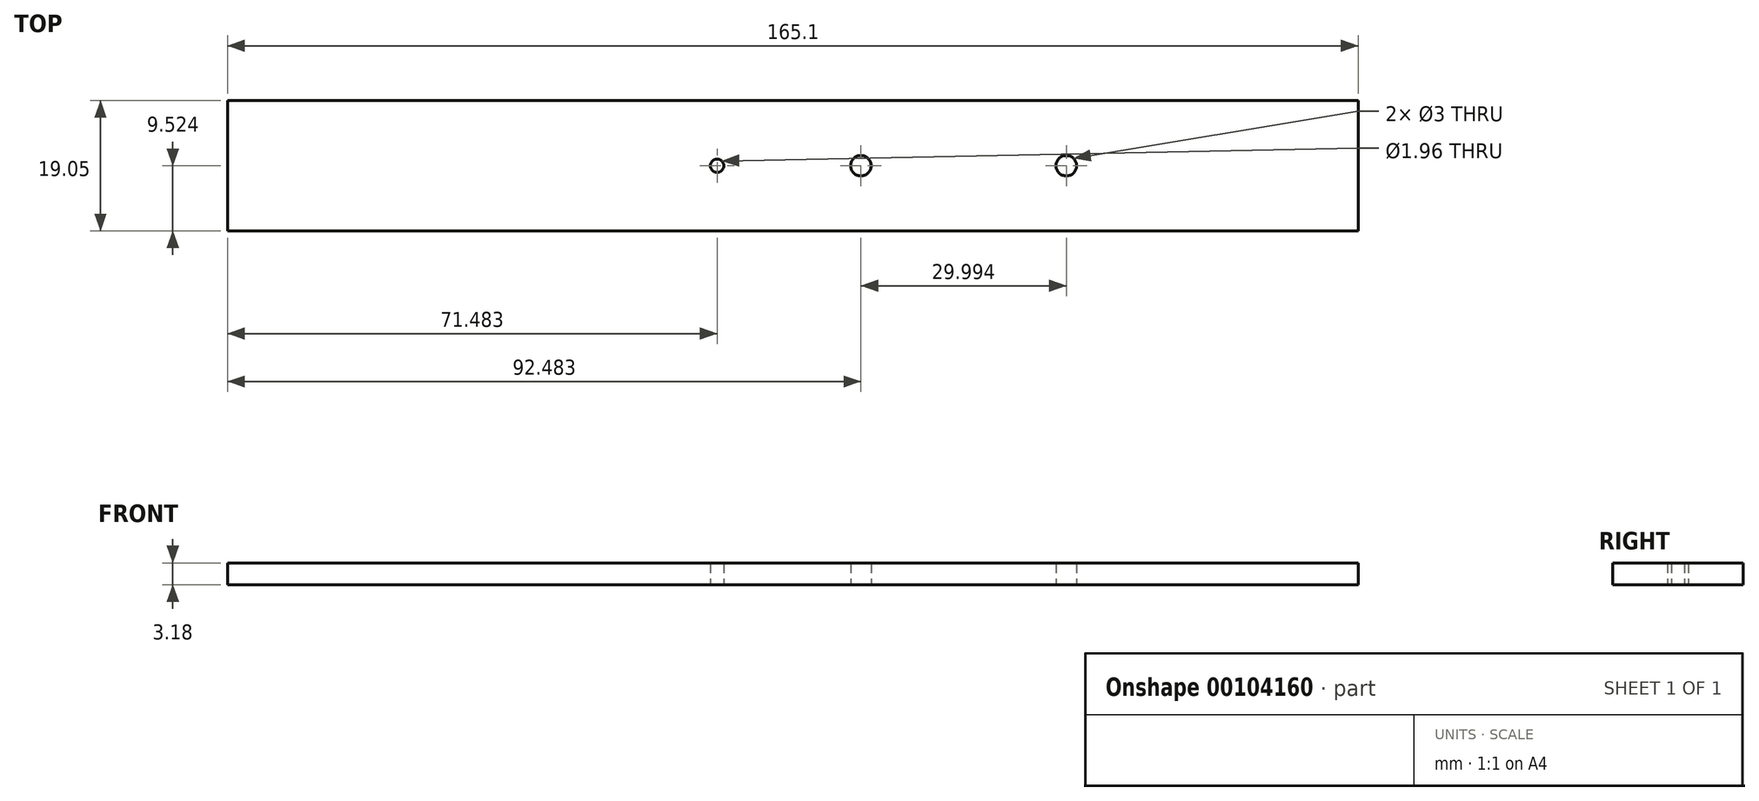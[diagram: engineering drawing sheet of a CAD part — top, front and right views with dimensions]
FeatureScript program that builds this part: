
annotation { "Feature Type Name" : "Feature", "Feature Type Description" : "" }
export const myFeature = defineFeature(function(context is Context, id is Id, definition is map)
    precondition{}
    {
        {
            var Q0;
            Q0=qCreatedBy(makeId("Top.planeOp"),FACE);
            var sketch = newSketch(context, id + "F0", { "sketchPlane" : qUnion([Q0])});
            skLineSegment(sketch, "E0.bottom", {"start": v(-131.62, -9.37) * mm, "end": v(33.48, -9.37) * mm});
            skLineSegment(sketch, "E0.top", {"start": v(-131.62, -28.42) * mm, "end": v(33.48, -28.42) * mm});
            skLineSegment(sketch, "E0.left", {"start": v(-131.62, -9.37) * mm, "end": v(-131.62, -28.42) * mm});
            skLineSegment(sketch, "E0.right", {"start": v(33.48, -9.37) * mm, "end": v(33.48, -28.42) * mm});
            skSolve(sketch);
        }
        {
            var Q0;
            Q0=makeQuery(id+"F0.imprint","IMPRINT",FACE,{"disambiguationData":[TD([[makeQuery(id+"F0.imprint","IMPRINT",EDGE,{"derivedFrom":sQuery(id+"F0.wireOp",EDGE,"E0.bottom")}),-1.0]])]});
            extrude(context, id + "F1", {"entities" : qUnion([Q0]), "depth" : 3.17 * mm});
        }
        {
            var Q0;
            Q0=makeQuery(id+"F1.opExtrude","CAP_FACE",FACE,{"disambiguationData":[OSD([sQuery(id+"F0.wireOp",EDGE,"E0.bottom"),sQuery(id+"F0.wireOp",EDGE,"E0.top"),sQuery(id+"F0.wireOp",EDGE,"E0.left"),sQuery(id+"F0.wireOp",EDGE,"E0.right")])],"isStart":true});
            var sketch = newSketch(context, id + "F2", { "sketchPlane" : qUnion([Q0])});
            skCircle(sketch, "E1", {"center": v(-39.14, 18.9) * mm, "radius": 1.5 * mm});
            skCircle(sketch, "E2", {"center": v(-60.14, 18.9) * mm, "radius": 0.98 * mm});
            skLineSegment(sketch, "E3.bottom", {"start": v(8.08, 12.93) * mm, "end": v(-14.14, 12.93) * mm});
            skLineSegment(sketch, "E3.top", {"start": v(8.08, 24.86) * mm, "end": v(-14.14, 24.86) * mm});
            skLineSegment(sketch, "E3.left", {"start": v(8.08, 12.93) * mm, "end": v(8.08, 24.86) * mm});
            skLineSegment(sketch, "E3.right", {"start": v(-14.14, 12.93) * mm, "end": v(-14.14, 24.86) * mm});
            skCircle(sketch, "E4", {"center": v(-9.14, 18.9) * mm, "radius": 1.5 * mm});
            skSolve(sketch);
        }
        {
            var Q0;
            Q0=makeQuery(id+"F2.imprint","IMPRINT",FACE,{"disambiguationData":[TD([[makeQuery(id+"F2.imprint","IMPRINT",EDGE,{"derivedFrom":sQuery(id+"F2.wireOp",EDGE,"E1")}),1.0]])]});
            extrude(context, id + "F3", {"entities" : qUnion([Q0]), "operationType" : NewBodyOperationType.REMOVE, "oppositeDirection" : true, "depth" : 25.4 * mm});
        }
        {
            var Q0;
            Q0=makeQuery(id+"F2.imprint","IMPRINT",FACE,{"disambiguationData":[TD([[makeQuery(id+"F2.imprint","IMPRINT",EDGE,{"derivedFrom":sQuery(id+"F2.wireOp",EDGE,"E2")}),1.0]])]});
            extrude(context, id + "F4", {"entities" : qUnion([Q0]), "operationType" : NewBodyOperationType.REMOVE, "oppositeDirection" : true, "depth" : 25.4 * mm});
        }
        {
            var Q0;
            Q0=makeQuery(id+"F2.imprint","IMPRINT",FACE,{"disambiguationData":[TD([[makeQuery(id+"F2.imprint","IMPRINT",EDGE,{"derivedFrom":sQuery(id+"F2.wireOp",EDGE,"E4")}),1.0]])]});
            extrude(context, id + "F5", {"entities" : qUnion([Q0]), "operationType" : NewBodyOperationType.REMOVE, "oppositeDirection" : true, "depth" : 25.4 * mm});
        }
    });
